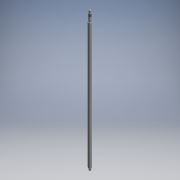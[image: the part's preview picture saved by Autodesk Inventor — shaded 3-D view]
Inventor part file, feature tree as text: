
AUTODESK INVENTOR PART (.ipt)
format: ipt  version: 2018 (Build 220112000, 112)  size: 123,392 bytes
history: native  units: mm
features: extrude x6, sketch x6, other x1, thread x1, chamfer x1
ambient origin geometry x8: Origin, YZ Plane, XZ Plane, XY Plane, X Axis, Y Axis, Z Axis, Center Point
bodies: Body1 (feature_tree)
feature tree (15):
  other  "Sólido1"
  extrude  "Extrusão1"  Depth=651.0mm TaperAngle=0.0deg
  extrude  "Extrusão2"  Depth=39.0mm TaperAngle=0.0deg
  extrude  "Extrusão3"  Depth=15.0mm TaperAngle=0.0deg
  extrude  "Extrusão4"  Depth=9.15mm TaperAngle=0.0deg
  extrude  "Extrusão5"  Depth=1.15mm TaperAngle=0.0deg
  extrude  "Extrusão6"  Depth=1.85mm TaperAngle=0.0deg
  thread  "Rosca1"  [1 undecoded]
  chamfer  "Chanfro1"  Distance=0.5mm Angle=45.0deg
  sketch  "Esboço1"  dims[d0=16.0mm d1=651.0mm d2=0.0mm]
  sketch  "Esboço2"  dims[d3=12.0mm d4=39.0mm d5=0.0mm]
  sketch  "Esboço3"  dims[d6=10.0mm d7=15.0mm d8=0.0mm]
  sketch  "Esboço4"  dims[d9=10.0mm d10=9.15mm d11=0.0mm]
  sketch  "Esboço5"  dims[d12=9.0mm d13=1.15mm d14=0.0mm]
  sketch  "Esboço6"  dims[d15=10.0mm d16=1.85mm d17=0.0mm d18=14.0mm d19=0.0mm d20=0.5mm d21=2.0mm d22=45.0deg]
note: 1 required parameter value undecoded (feature->parameter linkage not recoverable at this tier; creation-order binding heuristic only, values carry confidence <= 0.55)
